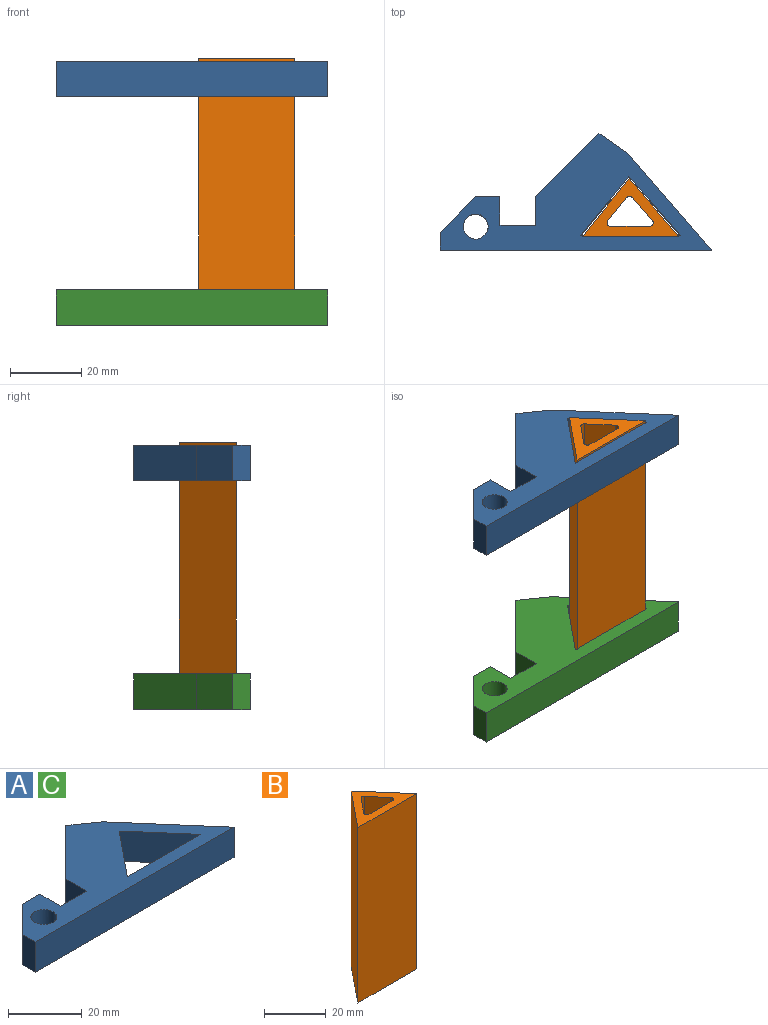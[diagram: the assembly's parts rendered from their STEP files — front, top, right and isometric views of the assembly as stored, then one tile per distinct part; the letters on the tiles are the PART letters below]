
ASSEMBLY  parts=3 mates=2
PART A: 16 faces, bbox 76.2x32.8x10 mm
  f0: plane 76.22x32.76mm, normal (0,0,1), area 985.2mm2, adj f2,f3,f4,f5,f6,f7,f8,f9
  f1: plane 76.22x32.76mm, normal (0,0,-1), area 985.2mm2, adj f2,f3,f4,f5,f6,f7,f8,f9
  f2: plane 10x6.79mm, normal (0,1,0), area 67.9mm2, adj f0,f1,f7,f10
  f3: plane 10x5mm, normal (-1,0,0), area 50mm2, adj f0,f1,f4,f10
  f4: plane 76.22x10mm, normal (0,-1,0), area 762.2mm2, adj f0,f1,f3,f11
  f5: plane 10x8.32mm, normal (0.57,0.82,0), area 101.5mm2, adj f0,f1,f6,f11
  f6: plane 17.76x17.76mm, normal (-0.71,0.71,0), area 251.1mm2, adj f0,f1,f5,f8
  f7: plane 10x8mm, normal (1,0,0), area 80mm2, adj f0,f1,f2,f9
  f8: plane 10x8mm, normal (-1,0,0), area 80mm2, adj f0,f1,f6,f9
  f9: plane 10x10mm, normal (0,1,0), area 100mm2, adj f0,f1,f7,f8
  f10: plane 10x10mm, normal (-0.71,0.71,0), area 141.4mm2, adj f0,f1,f2,f3
  f11: plane 26.93x23.35mm, normal (0.76,0.65,0), area 356.4mm2, adj f0,f1,f4,f5
  f12: plane 16.72x13.61mm, normal (0.78,-0.63,0), area 215.6mm2, adj f0,f1,f13,f14
  f13: plane 16.72x14.49mm, normal (-0.76,-0.65,0), area 221.2mm2, adj f0,f1,f12,f14
  f14: plane 28.1x10mm, normal (0,1,0), area 281mm2, adj f0,f1,f12,f13
  f15: cylinder r=3.5mm len=10mm, axis (0,0,-1), area 219.9mm2, adj f0,f1
PART B: 11 faces, bbox 27x16.1x69.5 mm
  f0: plane 69.48x16.05mm, normal (-0.78,0.63,0), area 1438.3mm2, adj f1,f2,f9,f10
  f1: plane 69.48x16.05mm, normal (0.76,0.65,0), area 1476mm2, adj f0,f2,f9,f10
  f2: plane 69.48x26.99mm, normal (0,-1,0), area 1875mm2, adj f0,f1,f9,f10
  f3: plane 69.48x6.5mm, normal (0.78,-0.63,0), area 582.3mm2, adj f6,f8,f9,f10
  f4: plane 69.48x6.5mm, normal (-0.76,-0.65,0), area 597.6mm2, adj f6,f7,f9,f10
  f5: plane 69.48x10.93mm, normal (0,1,0), area 759.1mm2, adj f7,f8,f9,f10
  f6: cylinder r=1mm len=69.48mm, axis (0,0,-1), area 121.2mm2, adj f3,f4,f9,f10
  f7: cylinder r=1mm len=69.48mm, axis (0,0,-1), area 158.8mm2, adj f4,f5,f9,f10
  f8: cylinder r=1mm len=69.48mm, axis (0,0,1), area 156.6mm2, adj f3,f5,f9,f10
  f9: plane 26.99x16.05mm, normal (0,0,1), area 150mm2, adj f0,f1,f2,f3,f4,f5,f6,f7
  f10: plane 26.99x16.05mm, normal (0,0,-1), area 150mm2, adj f0,f1,f2,f3,f4,f5,f6,f7
PART C: same geometry as A
PLACE A t=(-7.21,79.28,15.41)mm
PLACE B t=(-7.17,73.96,5.25)mm
PLACE C t=(-7.21,79.28,-48.71)mm
MATE slider A.f0 <-> B.f9  axis (0,0,1) through (15.18,83.36,4.21)mm
MATE slider B.f9 <-> C.f0  axis (0,0,1) through (15.18,83.36,4.99)mm
